# Revit family: AD-S112s - Yoke Mount
name_source: partatom
category: Generic Models
revit_build: Autodesk Revit 2014 (Build: 20130308_1515(x64)
units: mm (PartAtom-declared; Revit-internal decimal feet)

## types (1)
- AD-S112s - Yoke Mount
    Default Elevation = 1219 mm
    Depth = 323 mm
    Description = 12" Small Format Surface Mount Subwoofer
    Height = 594 mm
    Impedance = 8
    Manufacturer = QSC Audio Products, LLC
    Manufacturer URL = www.qscaudio.com
    Model = AD-S112s
    Mount Depth = 254 mm
    Mount Height = 596 mm  [stored 1.95538 ft]
    Mount Width = 115 mm
    Power Handling = 300
    Product Documentation Link = http://qsc.com
    Product Page URL = http://www.qsc.com
    Regulatory Compliance = IP54
    SPL Max = 121
    Sensitivity = 90
    URL = http://www.qsc.com
    Weight Dimensional (kg) = 19.6
    Weight Dimensional (lb) = 43.1
    Weight Product (kg) = 13.2
    Weight Product (lb) = 29
    Width = 354 mm  [stored 1.16142 ft]

note: [stored X ft] marks values corroborated as IEEE doubles in the binary element streams (Revit-internal decimal feet)

## geometry (parser evidence)
native form markers: Blend x3, Sweep x2
no freeform markers — native parametric forms only
